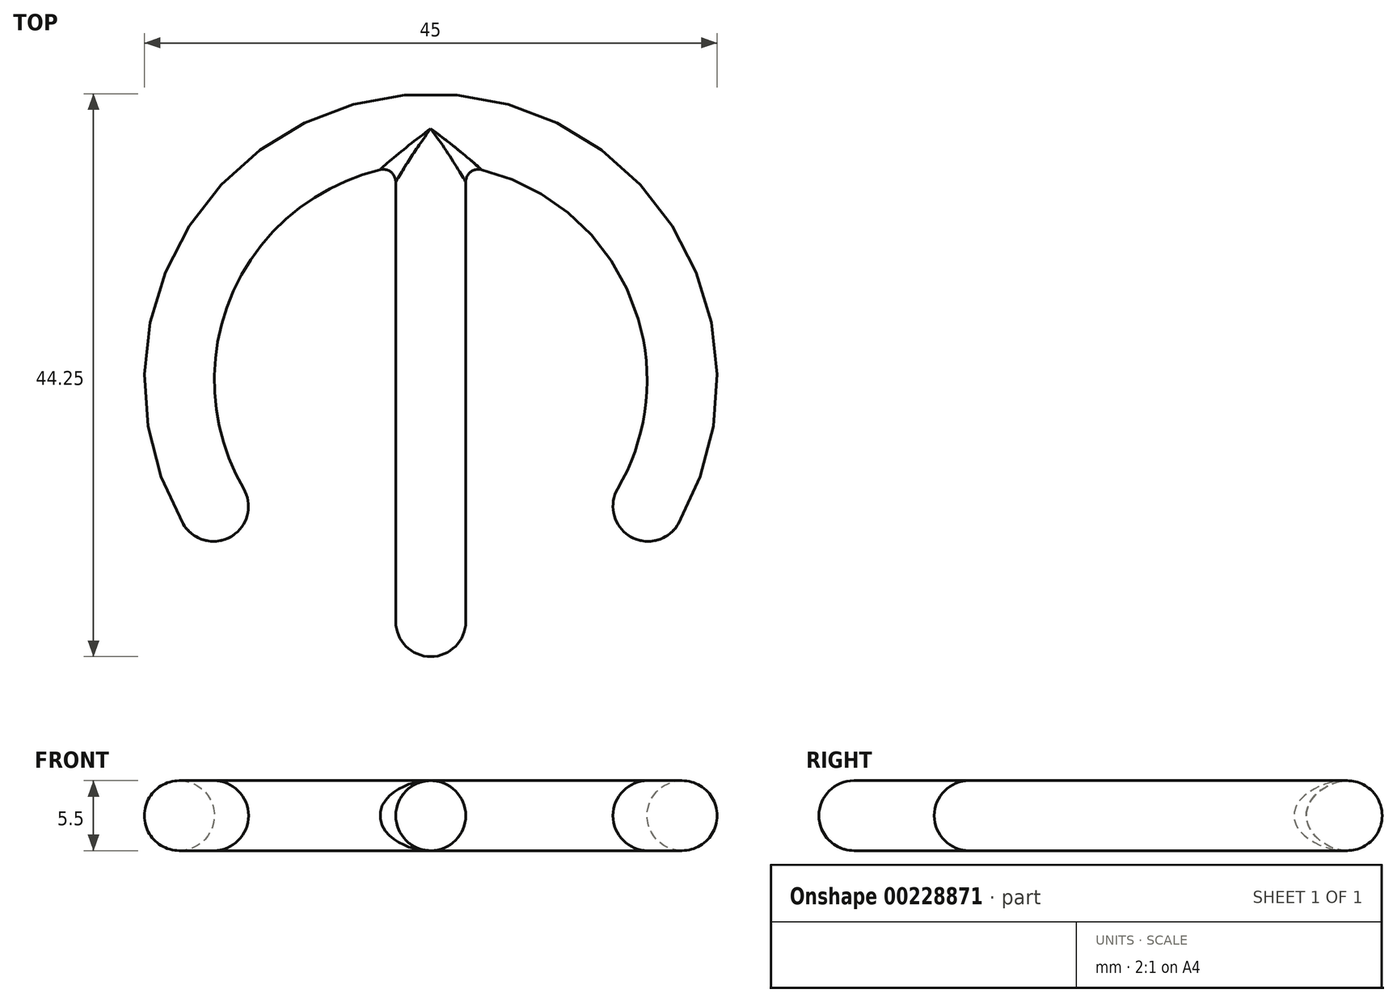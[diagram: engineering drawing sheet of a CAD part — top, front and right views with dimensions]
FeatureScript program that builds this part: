
annotation { "Feature Type Name" : "Feature", "Feature Type Description" : "" }
export const myFeature = defineFeature(function(context is Context, id is Id, definition is map)
    precondition{}
    {
        {
            var Q0;
            Q0=qCreatedBy(makeId("Top.planeOp"),FACE);
            var sketch = newSketch(context, id + "F0", { "sketchPlane" : qUnion([Q0])});
            skLineSegment(sketch, "E0", {"start": v(0, 0) * mm, "end": v(0, 39.5) * mm});
            skCircle(sketch, "E1", {"center": v(0, 19.75) * mm, "radius": 17.25 * mm, "construction": true});
            skArc(sketch, "E2", {"start": v(15.52, 7.53) * mm, "mid": v(14.3, 3.69) * mm, "end": v(15.93, 0) * mm});
            skArc(sketch, "E3", {"start": v(15.52, 7.53) * mm, "mid": v(17.77, 28.37) * mm, "end": v(0, 39.5) * mm});
            skPoint(sketch, "E4.visualSharp", {"position": v(0, 39.5) * mm});
            skArc(sketch, "E5", {"start": v(-15.93, 0) * mm, "mid": v(-14.3, 3.69) * mm, "end": v(-15.52, 7.53) * mm});
            skArc(sketch, "E6", {"start": v(0, 39.5) * mm, "mid": v(-17.77, 28.37) * mm, "end": v(-15.52, 7.53) * mm});
            skSolve(sketch);
        }
        {
            var Q0;
            Q0=qCreatedBy(makeId("Front.planeOp"),FACE);
            var sketch = newSketch(context, id + "F1", { "sketchPlane" : qUnion([Q0])});
            skCircle(sketch, "E7", {"center": v(0, 0) * mm, "radius": 2.75 * mm});
            skSolve(sketch);
        }
        {
            var Q0;
            Q0=qCreatedBy(makeId("Right.planeOp"),FACE);
            var sketch = newSketch(context, id + "F2", { "sketchPlane" : qUnion([Q0])});
            skCircle(sketch, "E8", {"center": v(39.5, 0) * mm, "radius": 2.75 * mm});
            skSolve(sketch);
        }
        {
            var Q0;
            Q0=makeQuery(id+"F2.imprint","IMPRINT",FACE,{"disambiguationData":[TD([[makeQuery(id+"F2.imprint","IMPRINT",EDGE,{"derivedFrom":sQuery(id+"F2.wireOp",EDGE,"E8")}),1.0]])]});
            var Q1;
            Q1=sQuery(id+"F0.wireOp",EDGE,"E3");
            sweep(context, id + "F3", {"profiles" : qUnion([Q0]), "path" : qUnion([Q1])});
        }
        {
            var Q0;
            Q0=makeQuery(id+"F3.opSweep","CAP_FACE",FACE,{"disambiguationData":[OSD([sQuery(id+"F0.wireOp",VERTEX,"E3.end"),sQuery(id+"F2.wireOp",EDGE,"E8")])],"isStart":true});
            var Q1;
            Q1=sQuery(id+"F0.wireOp",EDGE,"E6");
            sweep(context, id + "F4", {"operationType" : NewBodyOperationType.ADD, "profiles" : qUnion([Q0]), "path" : qUnion([Q1])});
        }
        {
            var Q0;
            Q0=makeQuery(id+"F1.imprint","IMPRINT",FACE,{"disambiguationData":[TD([[makeQuery(id+"F1.imprint","IMPRINT",EDGE,{"derivedFrom":sQuery(id+"F1.wireOp",EDGE,"E7")}),1.0]])]});
            var Q1;
            Q1=sQuery(id+"F0.wireOp",VERTEX,"E4.visualSharp");
            extrude(context, id + "F5", {"entities" : qUnion([Q0]), "operationType" : NewBodyOperationType.ADD, "endBound" : BoundingType.UP_TO_VERTEX, "oppositeDirection" : true, "endBoundEntityVertex" : qUnion([Q1]), "depth" : 25 * mm});
        }
        {
            var Q0;
            {var subQ0=sQuery(id+"F2.wireOp",EDGE,"E8");Q0=makeQuery(id+"F5.boolean.opBoolean","INTERSECT",EDGE,{"disambiguationData":[OD(0.0)],"derivedFrom":[makeQuery(id+"F4.boolean.opBoolean","MERGE",FACE,{"derivedFrom":[makeQuery(id+"F3.opSweep","SWEPT_FACE",FACE,{"disambiguationData":[OSD([sQuery(id+"F0.wireOp",EDGE,"E3"),subQ0])]}),makeQuery(id+"F4.opSweep","SWEPT_FACE",FACE,{"disambiguationData":[OSD([sQuery(id+"F0.wireOp",VERTEX,"E3.end"),sQuery(id+"F0.wireOp",EDGE,"E6"),subQ0])]})]}),makeQuery(id+"F5.opExtrude","SWEPT_FACE",FACE,{"disambiguationData":[OSD([sQuery(id+"F1.wireOp",EDGE,"E7")])]})]});}
            var Q1;
            {var subQ0=sQuery(id+"F2.wireOp",EDGE,"E8");Q1=makeQuery(id+"F5.boolean.opBoolean","INTERSECT",EDGE,{"disambiguationData":[OD(1.0)],"derivedFrom":[makeQuery(id+"F4.boolean.opBoolean","MERGE",FACE,{"derivedFrom":[makeQuery(id+"F3.opSweep","SWEPT_FACE",FACE,{"disambiguationData":[OSD([sQuery(id+"F0.wireOp",EDGE,"E3"),subQ0])]}),makeQuery(id+"F4.opSweep","SWEPT_FACE",FACE,{"disambiguationData":[OSD([sQuery(id+"F0.wireOp",VERTEX,"E3.end"),sQuery(id+"F0.wireOp",EDGE,"E6"),subQ0])]})]}),makeQuery(id+"F5.opExtrude","SWEPT_FACE",FACE,{"disambiguationData":[OSD([sQuery(id+"F1.wireOp",EDGE,"E7")])]})]});}
            fillet(context, id + "F6", {"entities" : qUnion([Q0, Q1]), "radius" : 1 * mm, "tangentPropagation" : true, "allowEdgeOverflow" : false});
        }
        {
            var Q0;
            Q0=makeQuery(id+"F5.opExtrude","CAP_FACE",FACE,{"disambiguationData":[OSD([sQuery(id+"F1.wireOp",EDGE,"E7")])],"isStart":true});
            extrude(context, id + "F7", {"entities" : qUnion([Q0]), "operationType" : NewBodyOperationType.ADD, "depth" : 2 * mm});
        }
        {
            var Q0;
            Q0=makeQuery(id+"F4.opSweep","CAP_EDGE",EDGE,{"disambiguationData":[OSD([sQuery(id+"F0.wireOp",VERTEX,"E3.end"),sQuery(id+"F0.wireOp",VERTEX,"E6.end"),sQuery(id+"F2.wireOp",EDGE,"E8")])],"isStart":false});
            var Q1;
            Q1=makeQuery(id+"F3.opSweep","CAP_EDGE",EDGE,{"disambiguationData":[OSD([sQuery(id+"F0.wireOp",VERTEX,"E3.start"),sQuery(id+"F2.wireOp",EDGE,"E8")])],"isStart":false});
            var Q2;
            Q2=makeQuery(id+"F7.opExtrude","CAP_EDGE",EDGE,{"disambiguationData":[OSD([sQuery(id+"F1.wireOp",EDGE,"E7")])],"isStart":false});
            fillet(context, id + "F8", {"entities" : qUnion([Q0, Q1, Q2]), "radius" : 2.75 * mm, "tangentPropagation" : true, "allowEdgeOverflow" : false});
        }
    });
